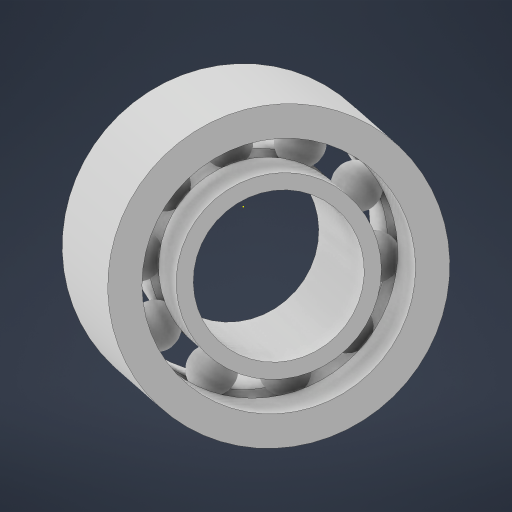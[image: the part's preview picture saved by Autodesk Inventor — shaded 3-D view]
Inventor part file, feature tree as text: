
AUTODESK INVENTOR PART (.ipt)
format: ipt  version: 2023 (Build 270158000, 158)  size: 378,880 bytes
history: native  units: mm
features: sketch x6, revolve x2, pattern_circular x1, sweep x1, hole x1
ambient origin geometry x8: Origin, YZ Plane, XZ Plane, XY Plane, X Axis, Y Axis, Z Axis, Center Point
bodies: Solid1 (feature_tree)
feature tree (11):
  revolve  "Revolution1"  [1 undecoded]
  revolve  "Revolution2"  [1 undecoded]
  sketch  "Sketch4"  dims[d8=90.0deg]
  pattern_circular  "Circular Pattern1"  Count=10 Angle=360.0deg
  sketch  "Sketch5"  dims[d9=3.0mm]
  sweep  "Sweep1"
  hole  "Hole1"  [1 undecoded]
  sketch  "Sketch2"  dims[d4=10.0mm d5=6.0mm]
  sketch  "Sketch3"  dims[d6=3.0mm d7=4.0mm]
  sketch  "Sketch7"  dims[d10=360.0deg d11=100.0mm d12=360.0deg]
  sketch  "Sketch8"  dims[d14=10.0mm d15=2.0mm d16=12.0mm d17=0.0mm d18=0.0mm d19=10.0mm d20=6.0mm d21=4.0mm d22=2.0mm d23=90.0deg d24=8.0mm d25=20.594885mm]
note: 3 required parameter values undecoded (feature->parameter linkage not recoverable at this tier; creation-order binding heuristic only, values carry confidence <= 0.55)